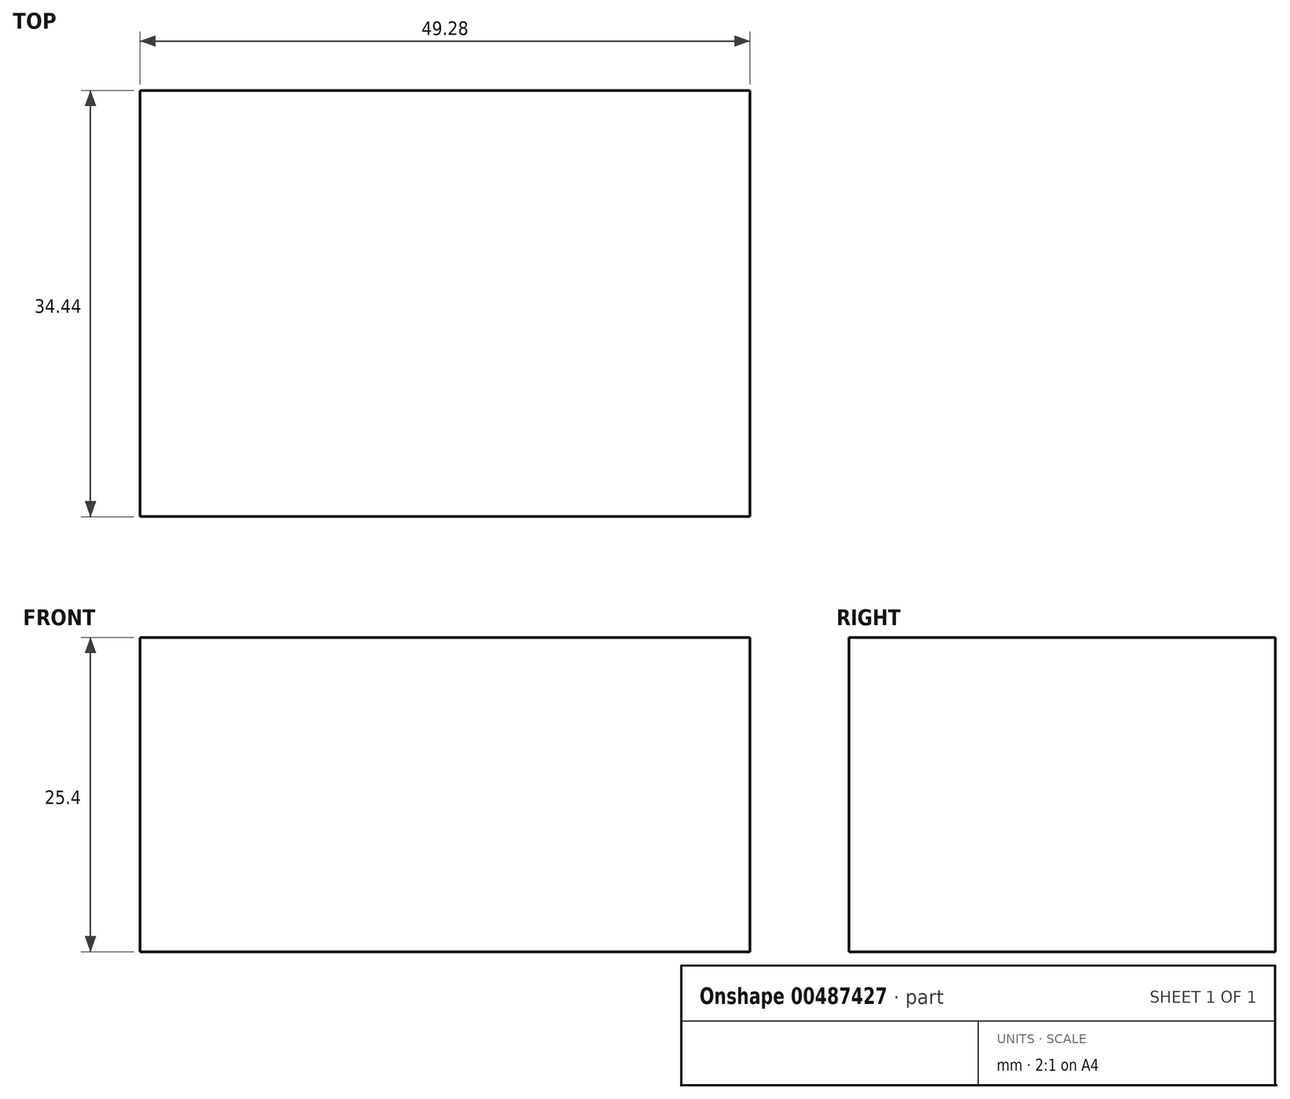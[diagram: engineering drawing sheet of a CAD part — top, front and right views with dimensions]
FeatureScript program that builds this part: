
annotation { "Feature Type Name" : "Feature", "Feature Type Description" : "" }
export const myFeature = defineFeature(function(context is Context, id is Id, definition is map)
    precondition{}
    {
        {
            var Q0;
            Q0=qCreatedBy(makeId("Top.planeOp"),FACE);
            var sketch = newSketch(context, id + "F0", { "sketchPlane" : qUnion([Q0])});
            skLineSegment(sketch, "E0.bottom", {"start": v(78.42, 80.8) * mm, "end": v(29.14, 80.8) * mm});
            skLineSegment(sketch, "E0.top", {"start": v(78.42, 46.36) * mm, "end": v(29.14, 46.36) * mm});
            skLineSegment(sketch, "E0.left", {"start": v(78.42, 80.8) * mm, "end": v(78.42, 46.36) * mm});
            skLineSegment(sketch, "E0.right", {"start": v(29.14, 80.8) * mm, "end": v(29.14, 46.36) * mm});
            skSolve(sketch);
        }
        {
            var Q0;
            Q0 = qSketchRegion(id + "F0", true);
            extrude(context, id + "F1", {"entities" : qUnion([Q0]), "depth" : 25.4 * mm});
        }
    });
